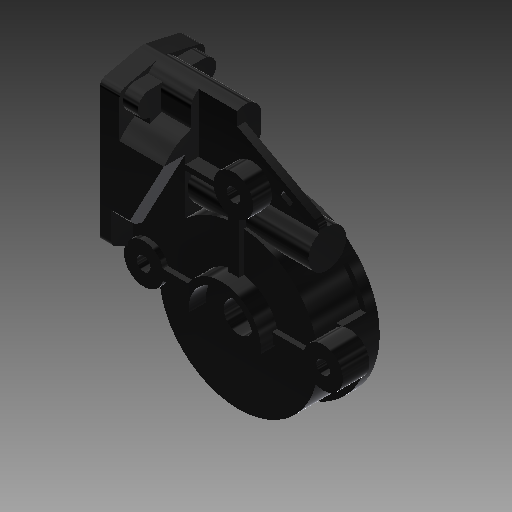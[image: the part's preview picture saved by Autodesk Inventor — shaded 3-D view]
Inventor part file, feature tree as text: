
AUTODESK INVENTOR PART (.ipt)
format: ipt  version: 2018 (Build 220112000, 112)  size: 318,976 bytes
history: native  units: in
note: dims shown in document units (in); Inventor stores cm internally (conversion verified against a paired STEP export)
features: fillet x1, other x1, imported_body x1
ambient origin geometry x8: Origin, YZ Plane, XZ Plane, XY Plane, X Axis, Y Axis, Z Axis, Center Point
bodies: Body1 (feature_tree)
feature tree (3):
  fillet  "Fillet1"  [1 undecoded]
  other  "AM-2235 gearbox housing.ipt1"
  imported_body  "Base1"
note: 1 required parameter value undecoded (feature->parameter linkage not recoverable at this tier; creation-order binding heuristic only, values carry confidence <= 0.55)
